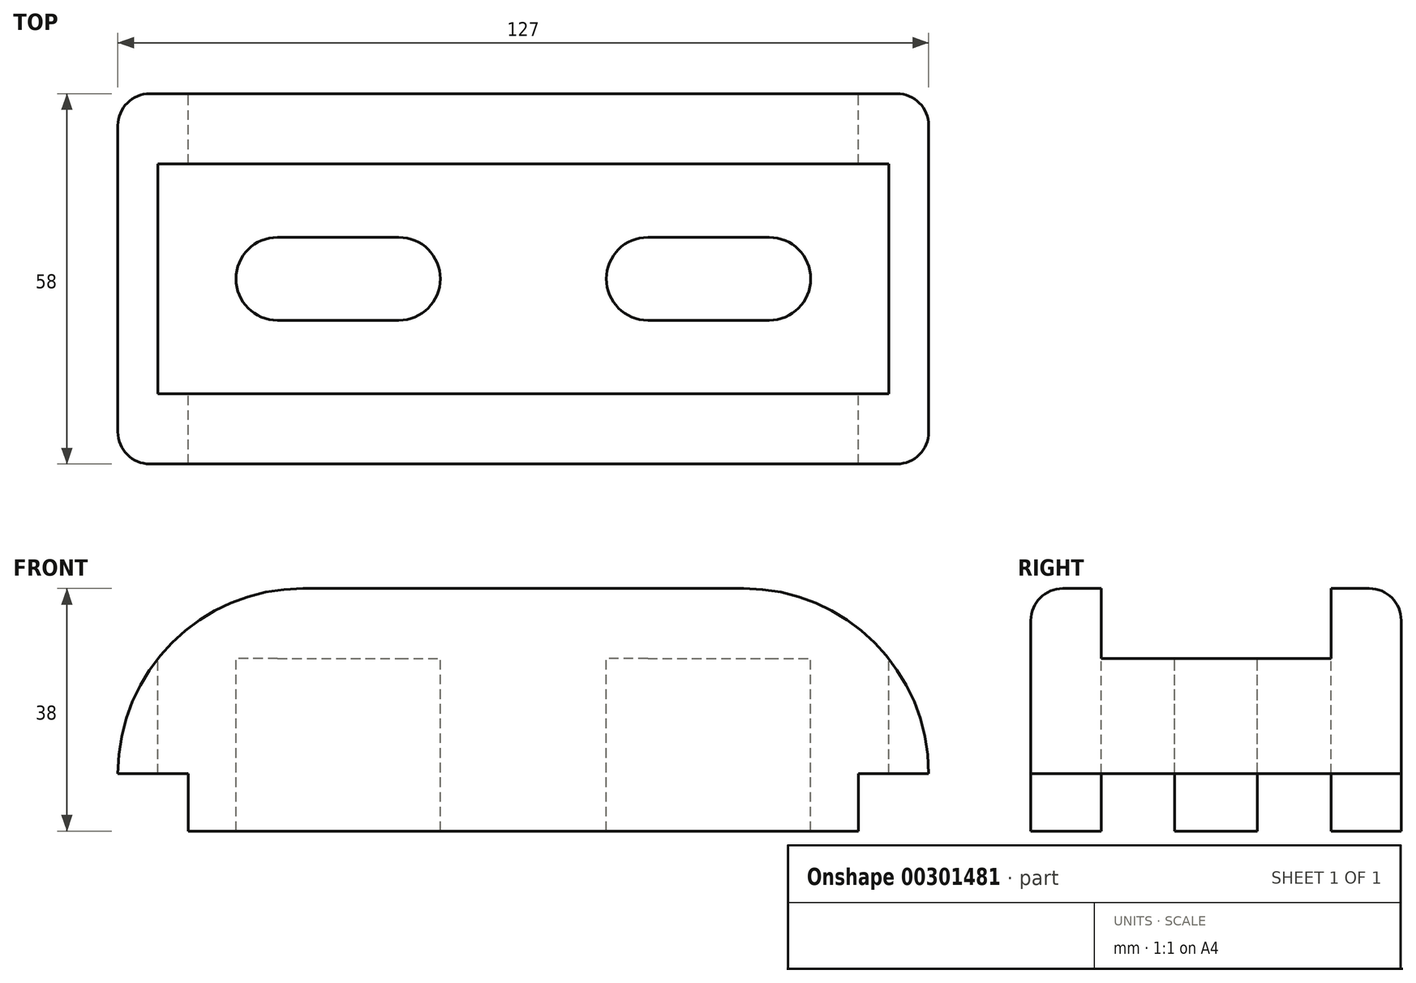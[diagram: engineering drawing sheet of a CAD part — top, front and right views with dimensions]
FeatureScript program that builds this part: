
annotation { "Feature Type Name" : "Feature", "Feature Type Description" : "" }
export const myFeature = defineFeature(function(context is Context, id is Id, definition is map)
    precondition{}
    {
        {
            var Q0;
            Q0=qCreatedBy(makeId("Front.planeOp"),FACE);
            var sketch = newSketch(context, id + "F0", { "sketchPlane" : qUnion([Q0])});
            skLineSegment(sketch, "E0.bottom", {"start": v(0, 0) * mm, "end": v(105, 0) * mm});
            skArc(sketch, "E1", {"start": v(18, 38) * mm, "mid": v(-2.5, 29.5) * mm, "end": v(-11, 9) * mm});
            skArc(sketch, "E2", {"start": v(116, 9) * mm, "mid": v(107.5, 29.5) * mm, "end": v(87, 38) * mm});
            skLineSegment(sketch, "E3", {"start": v(-11, 9) * mm, "end": v(116, 9) * mm, "construction": true});
            skLineSegment(sketch, "E4", {"start": v(52.5, 0) * mm, "end": v(52.5, 64.83) * mm, "construction": true});
            skLineSegment(sketch, "E5", {"start": v(-25.45, 38) * mm, "end": v(148.71, 38) * mm});
            skLineSegment(sketch, "E6", {"start": v(-11, 9) * mm, "end": v(0, 9) * mm});
            skLineSegment(sketch, "E7", {"start": v(0, 9) * mm, "end": v(0, 0) * mm});
            skLineSegment(sketch, "E8", {"start": v(105, 0) * mm, "end": v(105, 9) * mm});
            skLineSegment(sketch, "E9", {"start": v(105, 9) * mm, "end": v(116, 9) * mm});
            skLineSegment(sketch, "E10", {"start": v(-4.74, 27) * mm, "end": v(109.74, 27) * mm});
            skSolve(sketch);
        }
        {
            var Q0;
            Q0 = qSketchRegion(id + "F0", true);
            extrude(context, id + "F1", {"entities" : qUnion([Q0]), "endBound" : BoundingType.SYMMETRIC, "depth" : 58 * mm});
        }
        {
            var Q0;
            {var subQ3=sQuery(id+"F0.wireOp",EDGE,"E10");Q0=makeQuery(id+"F0.imprint","IMPRINT",FACE,{"disambiguationData":[TD([[makeQuery(id+"F0.imprint","IMPRINT",EDGE,{"derivedFrom":subQ3}),1.0]])]});}
            extrude(context, id + "F2", {"entities" : qUnion([Q0]), "operationType" : NewBodyOperationType.REMOVE, "endBound" : BoundingType.SYMMETRIC, "oppositeDirection" : true, "depth" : (58 - 22) * mm});
        }
        {
            var Q0;
            Q0=makeQuery(id+"F2.boolean.opBoolean","COPY",FACE,{"derivedFrom":makeQuery(id+"F2.opExtrude","SWEPT_FACE",FACE,{"disambiguationData":[OSD([sQuery(id+"F0.wireOp",EDGE,"E10")])]})});
            var sketch = newSketch(context, id + "F3", { "sketchPlane" : qUnion([Q0])});
            skLineSegment(sketch, "E11", {"start": v(14, 0) * mm, "end": v(33, 0) * mm, "construction": true});
            skLineSegment(sketch, "E12", {"start": v(72, 0) * mm, "end": v(91, 0) * mm, "construction": true});
            skArc(sketch, "E13.0.startCap", {"start": v(14, -6.5) * mm, "mid": v(7.5, 0) * mm, "end": v(14, 6.5) * mm});
            skArc(sketch, "E13.0.endCap", {"start": v(33, 6.5) * mm, "mid": v(39.5, 0) * mm, "end": v(33, -6.5) * mm});
            skLineSegment(sketch, "E13.0.left", {"start": v(14, 6.5) * mm, "end": v(33, 6.5) * mm});
            skLineSegment(sketch, "E13.0.right", {"start": v(14, -6.5) * mm, "end": v(33, -6.5) * mm});
            skArc(sketch, "E13.1.startCap", {"start": v(72, -6.5) * mm, "mid": v(65.5, 0) * mm, "end": v(72, 6.5) * mm});
            skArc(sketch, "E13.1.endCap", {"start": v(91, 6.5) * mm, "mid": v(97.5, 0) * mm, "end": v(91, -6.5) * mm});
            skLineSegment(sketch, "E13.1.left", {"start": v(72, 6.5) * mm, "end": v(91, 6.5) * mm});
            skLineSegment(sketch, "E13.1.right", {"start": v(72, -6.5) * mm, "end": v(91, -6.5) * mm});
            skLineSegment(sketch, "E14", {"start": v(52.5, -18) * mm, "end": v(52.5, 48.96) * mm, "construction": true});
            skSolve(sketch);
        }
        {
            var Q0;
            Q0=makeQuery(id+"F3.imprint","IMPRINT",FACE,{"disambiguationData":[TD([[makeQuery(id+"F3.imprint","IMPRINT",EDGE,{"derivedFrom":sQuery(id+"F3.wireOp",EDGE,"E13.0.startCap")}),-1.0]])]});
            var Q1;
            Q1=makeQuery(id+"F3.imprint","IMPRINT",FACE,{"disambiguationData":[TD([[makeQuery(id+"F3.imprint","IMPRINT",EDGE,{"derivedFrom":sQuery(id+"F3.wireOp",EDGE,"E13.1.startCap")}),-1.0]])]});
            extrude(context, id + "F4", {"entities" : qUnion([Q0, Q1]), "operationType" : NewBodyOperationType.REMOVE, "endBound" : BoundingType.THROUGH_ALL, "oppositeDirection" : true, "depth" : 25 * mm});
        }
        {
            var Q0;
            Q0=makeQuery(id+"F1.opExtrude","CAP_EDGE",EDGE,{"disambiguationData":[OSD([sQuery(id+"F0.wireOp",EDGE,"E2")])],"isStart":false});
            var Q1;
            Q1=makeQuery(id+"F1.opExtrude","CAP_EDGE",EDGE,{"disambiguationData":[OSD([sQuery(id+"F0.wireOp",EDGE,"E2")])],"isStart":true});
            fillet(context, id + "F5", {"entities" : qUnion([Q0, Q1]), "radius" : 5 * mm, "tangentPropagation" : true, "allowEdgeOverflow" : false});
        }
    });
